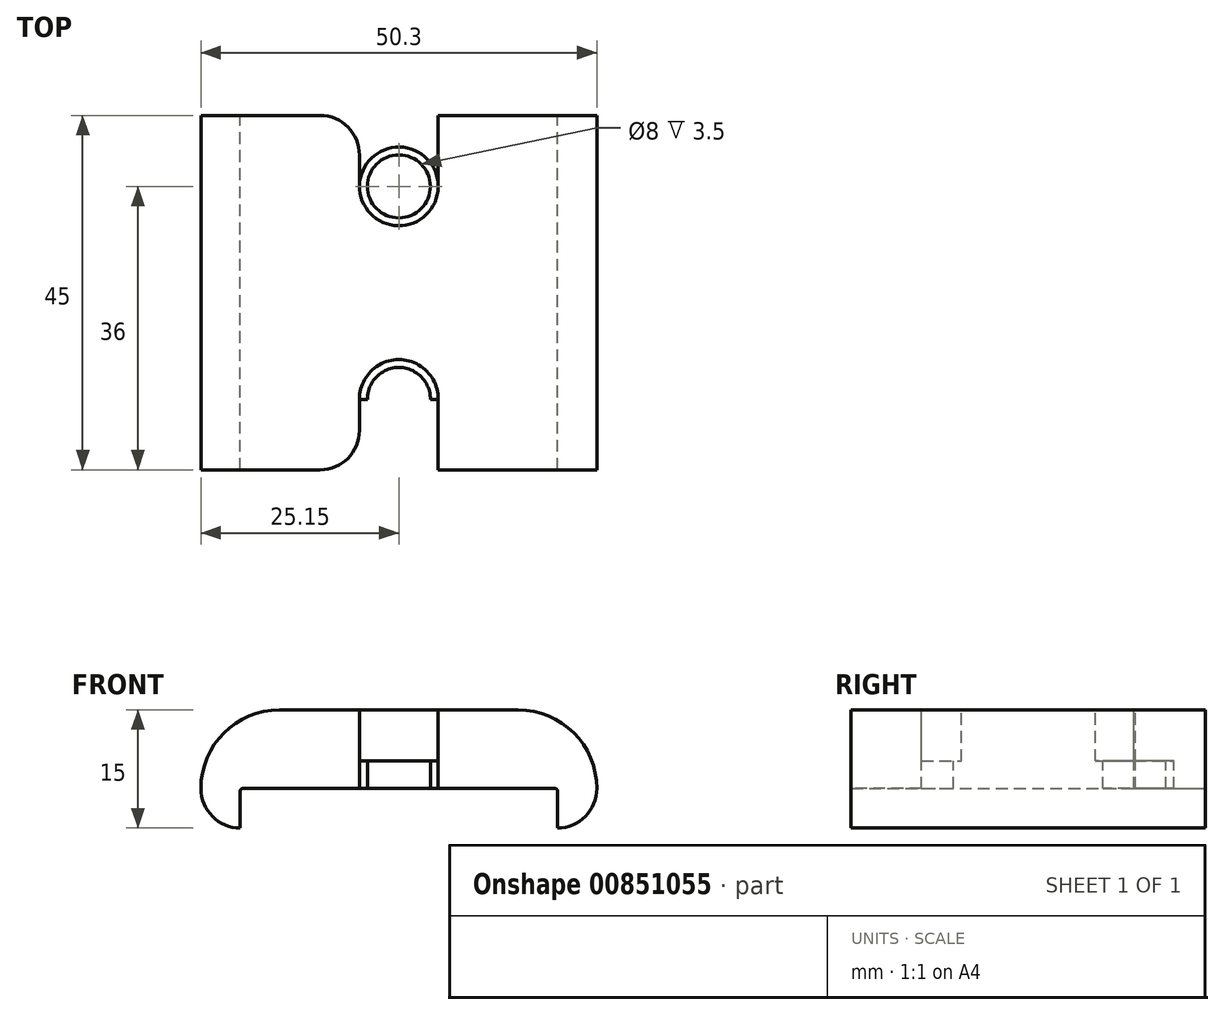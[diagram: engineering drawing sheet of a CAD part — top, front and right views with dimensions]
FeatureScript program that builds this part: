
annotation { "Feature Type Name" : "Feature", "Feature Type Description" : "" }
export const myFeature = defineFeature(function(context is Context, id is Id, definition is map)
    precondition{}
    {
        {
            var Q0;
            Q0=qCreatedBy(makeId("Front.planeOp"),FACE);
            var sketch = newSketch(context, id + "F0", { "sketchPlane" : qUnion([Q0])});
            skLineSegment(sketch, "E0.bottom", {"start": v(-25.15, 0.29) * mm, "end": v(25.15, 0.29) * mm});
            skLineSegment(sketch, "E0.top", {"start": v(-25.15, -14.71) * mm, "end": v(-20.15, -14.71) * mm});
            skLineSegment(sketch, "E0.left", {"start": v(-25.15, 0.29) * mm, "end": v(-25.15, -14.71) * mm});
            skLineSegment(sketch, "E0.right", {"start": v(25.15, 0.29) * mm, "end": v(25.15, -14.71) * mm});
            skLineSegment(sketch, "E1", {"start": v(-25.15, -14.71) * mm, "end": v(-20.15, -14.71) * mm, "construction": true});
            skLineSegment(sketch, "E2", {"start": v(-20.15, -14.71) * mm, "end": v(-20.15, -9.71) * mm, "construction": true});
            skLineSegment(sketch, "E3", {"start": v(-20.15, -9.71) * mm, "end": v(20.15, -9.71) * mm, "construction": true});
            skLineSegment(sketch, "E4", {"start": v(20.15, -9.71) * mm, "end": v(20.15, -14.71) * mm, "construction": true});
            skLineSegment(sketch, "E5.top", {"start": v(-20.15, -9.71) * mm, "end": v(20.15, -9.71) * mm});
            skLineSegment(sketch, "E5.left", {"start": v(-20.15, -14.71) * mm, "end": v(-20.15, -9.71) * mm});
            skLineSegment(sketch, "E5.right", {"start": v(20.15, -14.71) * mm, "end": v(20.15, -9.71) * mm});
            skLineSegment(sketch, "E6.trimOffspring", {"start": v(20.15, -14.71) * mm, "end": v(25.15, -14.71) * mm});
            skSolve(sketch);
        }
        {
            var Q0;
            Q0=makeQuery(id+"F0.imprint","IMPRINT",FACE,{"disambiguationData":[TD([[makeQuery(id+"F0.imprint","IMPRINT",EDGE,{"derivedFrom":sQuery(id+"F0.wireOp",EDGE,"E0.bottom")}),-1.0]])]});
            extrude(context, id + "F1", {"entities" : qUnion([Q0]), "endBound" : BoundingType.SYMMETRIC, "depth" : 45 * mm, "offsetDistance" : 25 * mm});
        }
        {
            var Q0;
            Q0=makeQuery(id+"F1.opExtrude","SWEPT_EDGE",EDGE,{"disambiguationData":[OSD([sQuery(id+"F0.wireOp",EDGE,"E5.top"),sQuery(id+"F0.wireOp",EDGE,"E5.left")])]});
            var Q1;
            Q1=makeQuery(id+"F1.opExtrude","SWEPT_EDGE",EDGE,{"disambiguationData":[OSD([sQuery(id+"F0.wireOp",EDGE,"E5.top"),sQuery(id+"F0.wireOp",EDGE,"E5.right")])]});
            fillet(context, id + "F2", {"entities" : qUnion([Q0, Q1]), "tangentPropagation" : true, "radius" : 0.3 * mm, "defaultsChanged" : true, "vertexSettings" : [], "allowEdgeOverflow" : false});
        }
        {
            var Q0;
            Q0=makeQuery(id+"F1.opExtrude","SWEPT_FACE",FACE,{"disambiguationData":[OSD([sQuery(id+"F0.wireOp",EDGE,"E0.bottom")])]});
            var sketch = newSketch(context, id + "F3", { "sketchPlane" : qUnion([Q0])});
            skLineSegment(sketch, "E7", {"start": v(0, -22.5) * mm, "end": v(0, -13.5) * mm, "construction": true});
            skLineSegment(sketch, "E8", {"start": v(0, -13.5) * mm, "end": v(0, 13.5) * mm, "construction": true});
            skCircle(sketch, "E9", {"center": v(0, 13.5) * mm, "radius": 4 * mm});
            skCircle(sketch, "E10", {"center": v(0, -13.5) * mm, "radius": 4 * mm});
            skSolve(sketch);
        }
        {
            var Q0;
            Q0=makeQuery(id+"F3.imprint","IMPRINT",FACE,{"disambiguationData":[TD([[makeQuery(id+"F3.imprint","IMPRINT",EDGE,{"derivedFrom":sQuery(id+"F3.wireOp",EDGE,"E9")}),1.0]])]});
            var Q1;
            Q1=makeQuery(id+"F3.imprint","IMPRINT",FACE,{"disambiguationData":[TD([[makeQuery(id+"F3.imprint","IMPRINT",EDGE,{"derivedFrom":sQuery(id+"F3.wireOp",EDGE,"E10")}),1.0]])]});
            extrude(context, id + "F4", {"entities" : qUnion([Q0, Q1]), "operationType" : NewBodyOperationType.REMOVE, "oppositeDirection" : true, "depth" : 25 * mm, "offsetDistance" : 25 * mm});
        }
        {
            var Q0;
            Q0=makeQuery(id+"F1.opExtrude","SWEPT_FACE",FACE,{"disambiguationData":[OSD([sQuery(id+"F0.wireOp",EDGE,"E0.bottom")])]});
            var sketch = newSketch(context, id + "F5", { "sketchPlane" : qUnion([Q0])});
            skCircle(sketch, "E11", {"center": v(0, 13.5) * mm, "radius": 5 * mm});
            skCircle(sketch, "E12", {"center": v(0, -13.5) * mm, "radius": 5 * mm});
            skSolve(sketch);
        }
        {
            var Q0;
            Q0=makeQuery(id+"F5.imprint","IMPRINT",FACE,{"disambiguationData":[TD([[makeQuery(id+"F5.imprint","IMPRINT",EDGE,{"derivedFrom":sQuery(id+"F5.wireOp",EDGE,"E11")}),1.0]])]});
            var Q1;
            Q1=makeQuery(id+"F5.imprint","IMPRINT",FACE,{"disambiguationData":[TD([[makeQuery(id+"F5.imprint","IMPRINT",EDGE,{"derivedFrom":sQuery(id+"F5.wireOp",EDGE,"E12")}),1.0]])]});
            extrude(context, id + "F6", {"entities" : qUnion([Q0, Q1]), "operationType" : NewBodyOperationType.REMOVE, "oppositeDirection" : true, "depth" : 6.5 * mm, "offsetDistance" : 25 * mm});
        }
        {
            var Q0;
            Q0=makeQuery(id+"F1.opExtrude","SWEPT_BODY",BODY,{"disambiguationData":[OSD([sQuery(id+"F0.wireOp",EDGE,"E0.bottom"),sQuery(id+"F0.wireOp",EDGE,"E0.top"),sQuery(id+"F0.wireOp",EDGE,"E0.left"),sQuery(id+"F0.wireOp",EDGE,"E0.right"),sQuery(id+"F0.wireOp",EDGE,"E5.top"),sQuery(id+"F0.wireOp",EDGE,"E5.left"),sQuery(id+"F0.wireOp",EDGE,"E5.right"),sQuery(id+"F0.wireOp",EDGE,"E6.trimOffspring")])]});
            transform(context, id + "F7", {"entities" : qUnion([Q0]), "transformType" : TransformType.TRANSLATION_3D, "dx" : 0 * mm, "dy" : 0 * mm, "dz" : -0.3 * mm, "makeCopy" : false});
        }
        {
            var Q0;
            Q0=makeQuery(id+"F1.opExtrude","SWEPT_FACE",FACE,{"disambiguationData":[OSD([sQuery(id+"F0.wireOp",EDGE,"E0.bottom")])]});
            var sketch = newSketch(context, id + "F8", { "sketchPlane" : qUnion([Q0])});
            skLineSegment(sketch, "E13.bottom", {"start": v(-5, 13.4) * mm, "end": v(5, 13.4) * mm});
            skLineSegment(sketch, "E13.top", {"start": v(-5, 23.4) * mm, "end": v(5, 23.4) * mm});
            skLineSegment(sketch, "E13.left", {"start": v(-5, 13.4) * mm, "end": v(-5, 23.4) * mm});
            skLineSegment(sketch, "E13.right", {"start": v(5, 13.4) * mm, "end": v(5, 23.4) * mm});
            skLineSegment(sketch, "E14.bottom", {"start": v(-5, -13.57) * mm, "end": v(5, -13.57) * mm});
            skLineSegment(sketch, "E14.top", {"start": v(-5, -23.57) * mm, "end": v(5, -23.57) * mm});
            skLineSegment(sketch, "E14.left", {"start": v(-5, -13.57) * mm, "end": v(-5, -23.57) * mm});
            skLineSegment(sketch, "E14.right", {"start": v(5, -13.57) * mm, "end": v(5, -23.57) * mm});
            skSolve(sketch);
        }
        {
            var Q0;
            {var subQ3=sQuery(id+"F8.wireOp",EDGE,"E14.right");var subQ5=sQuery(id+"F8.wireOp",EDGE,"E14.bottom");var subQ8=makeQuery(id+"F8.imprint","INTERSECT",VERTEX,{"derivedFrom":[subQ5,subQ3]});Q0=makeQuery(id+"F8.imprint","IMPRINT",FACE,{"disambiguationData":[TD([[makeQuery(id+"F8.imprint","IMPRINT",EDGE,{"disambiguationData":[TD([[subQ8,1.0]])],"derivedFrom":subQ5}),-1.0]])]});}
            var Q1;
            {var subQ0=sQuery(id+"F8.wireOp",EDGE,"E14.bottom");var subQ1=makeQuery(id+"F6.boolean.opBoolean","COPY",EDGE,{"derivedFrom":makeQuery(id+"F6.opExtrude","CAP_EDGE",EDGE,{"disambiguationData":[OSD([sQuery(id+"F5.wireOp",EDGE,"E12")])],"isStart":true})});var subQ3=makeQuery(id+"F8.imprint","INTERSECT",VERTEX,{"derivedFrom":[subQ1,subQ0]});Q1=makeQuery(id+"F8.imprint","IMPRINT",FACE,{"disambiguationData":[TD([[makeQuery(id+"F8.imprint","IMPRINT",EDGE,{"disambiguationData":[TD([[subQ3,1.0]])],"derivedFrom":subQ0}),-1.0]])]});}
            var Q2;
            {var subQ3=sQuery(id+"F8.wireOp",EDGE,"E13.right");var subQ7=sQuery(id+"F8.wireOp",EDGE,"E13.bottom");var subQ8=makeQuery(id+"F8.imprint","INTERSECT",VERTEX,{"derivedFrom":[subQ7,subQ3]});Q2=makeQuery(id+"F8.imprint","IMPRINT",FACE,{"disambiguationData":[TD([[makeQuery(id+"F8.imprint","IMPRINT",EDGE,{"disambiguationData":[TD([[subQ8,1.0]])],"derivedFrom":subQ7}),1.0]])]});}
            var Q3;
            {var subQ1=sQuery(id+"F8.wireOp",EDGE,"E13.bottom");var subQ2=makeQuery(id+"F6.boolean.opBoolean","COPY",EDGE,{"derivedFrom":makeQuery(id+"F6.opExtrude","CAP_EDGE",EDGE,{"disambiguationData":[OSD([sQuery(id+"F5.wireOp",EDGE,"E11")])],"isStart":true})});var subQ4=makeQuery(id+"F8.imprint","INTERSECT",VERTEX,{"derivedFrom":[subQ2,subQ1]});Q3=makeQuery(id+"F8.imprint","IMPRINT",FACE,{"disambiguationData":[TD([[makeQuery(id+"F8.imprint","IMPRINT",EDGE,{"disambiguationData":[TD([[subQ4,-1.0]])],"derivedFrom":subQ2}),1.0]])]});}
            extrude(context, id + "F9", {"entities" : qUnion([Q0, Q1, Q2, Q3]), "operationType" : NewBodyOperationType.REMOVE, "oppositeDirection" : true, "depth" : 25 * mm, "offsetDistance" : 25 * mm});
        }
        {
            var Q0;
            Q0=makeQuery(id+"F1.opExtrude","SWEPT_EDGE",EDGE,{"disambiguationData":[OSD([sQuery(id+"F0.wireOp",EDGE,"E0.bottom"),sQuery(id+"F0.wireOp",EDGE,"E0.left")])]});
            var Q1;
            Q1=makeQuery(id+"F1.opExtrude","SWEPT_EDGE",EDGE,{"disambiguationData":[OSD([sQuery(id+"F0.wireOp",EDGE,"E0.bottom"),sQuery(id+"F0.wireOp",EDGE,"E0.right")])]});
            fillet(context, id + "F10", {"entities" : qUnion([Q0, Q1]), "tangentPropagation" : true, "radius" : 10 * mm, "defaultsChanged" : true, "vertexSettings" : [], "allowEdgeOverflow" : false});
        }
        {
            var Q0;
            Q0=makeQuery(id+"F1.opExtrude","SWEPT_EDGE",EDGE,{"disambiguationData":[OSD([sQuery(id+"F0.wireOp",EDGE,"E0.right"),sQuery(id+"F0.wireOp",EDGE,"E6.trimOffspring")])]});
            var Q1;
            Q1=makeQuery(id+"F1.opExtrude","SWEPT_EDGE",EDGE,{"disambiguationData":[OSD([sQuery(id+"F0.wireOp",EDGE,"E0.top"),sQuery(id+"F0.wireOp",EDGE,"E0.left")])]});
            fillet(context, id + "F11", {"entities" : qUnion([Q0, Q1]), "tangentPropagation" : true, "radius" : 5 * mm, "defaultsChanged" : false, "vertexSettings" : [], "allowEdgeOverflow" : false});
        }
        {
            var Q0;
            Q0=makeQuery(id+"F9.boolean.opBoolean","COPY",EDGE,{"derivedFrom":makeQuery(id+"F9.opExtrude","SWEPT_EDGE",EDGE,{"disambiguationData":[OSD([sQuery(id+"F0.wireOp",EDGE,"E0.bottom"),sQuery(id+"F8.wireOp",EDGE,"E14.left")])]})});
            var Q1;
            Q1=makeQuery(id+"F9.boolean.opBoolean","COPY",EDGE,{"derivedFrom":makeQuery(id+"F9.opExtrude","SWEPT_EDGE",EDGE,{"disambiguationData":[OSD([sQuery(id+"F0.wireOp",EDGE,"E0.bottom"),sQuery(id+"F8.wireOp",EDGE,"E14.right")])]})});
            var Q2;
            Q2=makeQuery(id+"F9.boolean.opBoolean","COPY",EDGE,{"derivedFrom":makeQuery(id+"F9.opExtrude","SWEPT_EDGE",EDGE,{"disambiguationData":[OSD([sQuery(id+"F0.wireOp",EDGE,"E0.bottom"),sQuery(id+"F8.wireOp",EDGE,"E13.right")])]})});
            var Q3;
            Q3=makeQuery(id+"F9.boolean.opBoolean","COPY",EDGE,{"derivedFrom":makeQuery(id+"F9.opExtrude","SWEPT_EDGE",EDGE,{"disambiguationData":[OSD([sQuery(id+"F0.wireOp",EDGE,"E0.bottom"),sQuery(id+"F8.wireOp",EDGE,"E13.left")])]})});
            fillet(context, id + "F12", {"entities" : qUnion([Q0, Q1, Q2, Q3]), "tangentPropagation" : true, "radius" : 5 * mm, "defaultsChanged" : false, "vertexSettings" : [], "allowEdgeOverflow" : false});
        }
    });
